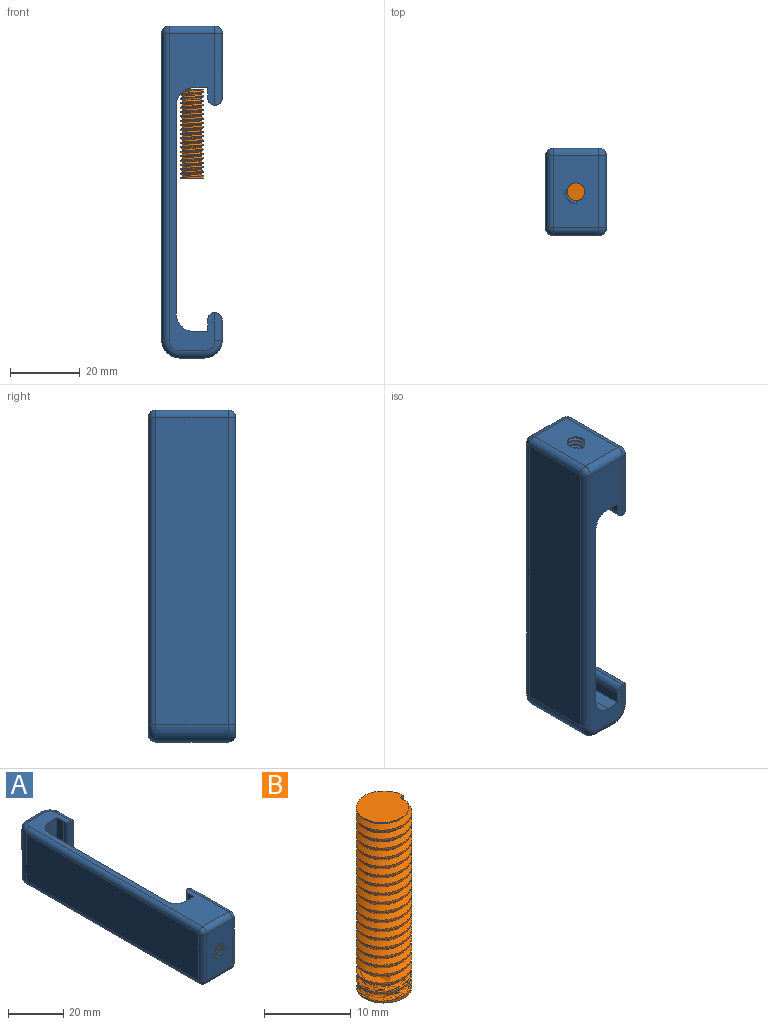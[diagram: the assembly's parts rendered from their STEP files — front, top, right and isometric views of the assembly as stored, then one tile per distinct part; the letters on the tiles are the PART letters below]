
ASSEMBLY  parts=2 mates=1
PART A: 48 faces, bbox 18.6x96.9x25.4 mm
  f0: cylinder r=2.55mm len=17.93mm, axis (0,-1,0), area 124.8mm2, adj f2,f3,f14,f42,f44,f45
  f1: cylinder r=2.55mm len=2.84mm, axis (0,-1,0), area 0mm2, adj f2,f43
  f2: cylinder r=5mm len=25mm, axis (0,0,-1), area 180.8mm2, adj f0,f1,f3,f4,f18,f19,f43,f44
  f3: plane 25.4x4.4mm, normal (0,1,0), area 89.6mm2, adj f0,f2,f17,f18,f19,f44,f45
  f4: plane 60x25mm, normal (1,0,0), area 1500mm2, adj f2,f5,f18,f19
  f5: cylinder r=5mm len=25mm, axis (0,0,-1), area 196.3mm2, adj f4,f6,f18,f19
  f6: plane 25x4mm, normal (0,-1,0), area 100mm2, adj f5,f7,f18,f19
  f7: plane 25x3.34mm, normal (-1,0,0), area 83.5mm2, adj f6,f18,f19,f46
  f8: plane 25x0.08mm, normal (0,-1,0), area 2.1mm2, adj f18,f19,f24,f46
  f9: plane 20.8x5.9mm, normal (1,0,0), area 122.6mm2, adj f10,f21,f24,f28
  f10: cylinder r=5mm len=20.8mm, axis (0,0,-1), area 163.4mm2, adj f9,f11,f20,f33
  f11: plane 20.8x7.37mm, normal (0,1,0), area 153.2mm2, adj f10,f12,f22,f36
  f12: cylinder r=5mm len=20.8mm, axis (0,0,-1), area 163.4mm2, adj f11,f13,f25,f39
  f13: plane 88.29x20.8mm, normal (-1,0,0), area 1836.4mm2, adj f12,f29,f37,f41
  f14: plane 20.8x13.17mm, normal (0,-1,0), area 251mm2, adj f0,f30,f31,f37,f38,f42,f44
  f15: plane 20.8x18.54mm, normal (1,0,0), area 385.5mm2, adj f23,f27,f31,f32
  f16: plane 25x0.08mm, normal (0,1,0), area 2.1mm2, adj f18,f19,f27,f47
  f17: plane 25x3mm, normal (-1,0,0), area 75mm2, adj f3,f18,f19,f47
  f18: plane 91.19x13.17mm, normal (0,0,1), area 451.7mm2, adj f2,f3,f4,f5,f6,f7,f8,f16
  f19: plane 91.19x13.17mm, normal (0,0,-1), area 451.7mm2, adj f2,f3,f4,f5,f6,f7,f8,f16
  f20: torus R=2.9mm, axis (0,0,1), area 22mm2, adj f10,f18,f21,f22
  f21: cylinder r=2.1mm len=8mm, axis (0,-1,0), area 22.9mm2, adj f9,f18,f20,f24
  f22: cylinder r=2.1mm len=7.37mm, axis (1,0,0), area 24.3mm2, adj f11,f18,f20,f25
  f23: cylinder r=2.1mm len=20.64mm, axis (0,-1,0), area 64.6mm2, adj f15,f18,f26,f27
  f24: cylinder r=2.1mm len=25mm, axis (0,0,1), area 75.5mm2, adj f8,f9,f21,f28
  f25: torus R=2.9mm, axis (0,0,1), area 22mm2, adj f12,f18,f22,f29
  f26: sphere r=2.1mm, area 6.9mm2, adj f23,f30,f31
  f27: cylinder r=2.1mm len=25mm, axis (0,0,-1), area 75.5mm2, adj f15,f16,f23,f32
  f28: cylinder r=2.1mm len=8mm, axis (0,1,0), area 22.9mm2, adj f9,f19,f24,f33
  f29: cylinder r=2.1mm len=88.29mm, axis (0,1,0), area 291.2mm2, adj f13,f18,f25,f34
  f30: cylinder r=2.1mm len=13.17mm, axis (-1,0,0), area 43.4mm2, adj f14,f18,f26,f34
  f31: cylinder r=2.1mm len=20.8mm, axis (0,0,1), area 68.6mm2, adj f14,f15,f26,f35
  f32: cylinder r=2.1mm len=20.64mm, axis (0,1,0), area 64.6mm2, adj f15,f19,f27,f35
  f33: torus R=2.9mm, axis (0,0,1), area 22mm2, adj f10,f19,f28,f36
  f34: sphere r=2.1mm, area 6.9mm2, adj f29,f30,f37
  f35: sphere r=2.1mm, area 6.9mm2, adj f31,f32,f38
  f36: cylinder r=2.1mm len=7.37mm, axis (-1,0,0), area 24.3mm2, adj f11,f19,f33,f39
  f37: cylinder r=2.1mm len=20.8mm, axis (0,0,-1), area 68.6mm2, adj f13,f14,f34,f40
  f38: cylinder r=2.1mm len=13.17mm, axis (1,0,0), area 43.4mm2, adj f14,f19,f35,f40
  f39: torus R=2.9mm, axis (0,0,1), area 22mm2, adj f12,f19,f36,f41
  f40: sphere r=2.1mm, area 6.9mm2, adj f37,f38,f41
  f41: cylinder r=2.1mm len=88.29mm, axis (0,-1,0), area 291.2mm2, adj f13,f19,f39,f40
  f42: plane 0.88x0.39mm, normal (-1,0,0), area 0.2mm2, adj f0,f14,f44,f45
  f43: bspline ~6.86x3.96mm, area 5.2mm2, adj f1,f2,f44
  f44: bspline ~19.1x7.92mm, area 262.1mm2, adj f0,f2,f3,f14,f42,f43,f45
  f45: bspline ~18.37x7.92mm, area 248.3mm2, adj f0,f3,f42,f44
  f46: cylinder r=2mm len=25mm, axis (0,0,-1), area 78.5mm2, adj f7,f8,f18,f19
  f47: cylinder r=2mm len=25mm, axis (0,0,1), area 78.5mm2, adj f16,f17,f18,f19
PART B: 7 faces, bbox 7x8x27 mm
  f0: cylinder r=3.2mm len=25.4mm, axis (0,0,-1), area 154.9mm2, adj f1,f2,f3,f4,f5,f6
  f1: plane 6.76x6.57mm, normal (0,0,1), area 30.2mm2, adj f0,f3,f4
  f2: plane 6.76x6.57mm, normal (0,0,-1), area 30.2mm2, adj f0,f5,f6
  f3: plane 0.52x0.51mm, normal (0,-1,0), area 0.1mm2, adj f0,f1,f6
  f4: bspline ~26.04x7.67mm, area 267.6mm2, adj f0,f1,f5,f6
  f5: plane 0.52x0.51mm, normal (0,1,0), area 0.1mm2, adj f0,f2,f4
  f6: bspline ~26.03x7.67mm, area 266.2mm2, adj f0,f2,f3,f4
PLACE A rot(axis=(-1,0,0),90deg) t=(-44.16,-34.29,-34.47)mm
PLACE B t=(-44.16,-21.79,-25.48)mm
MATE fastened A.f0 <-> B.f0  axis (0,0,1) through (-44.16,-21.79,-0.08)mm
